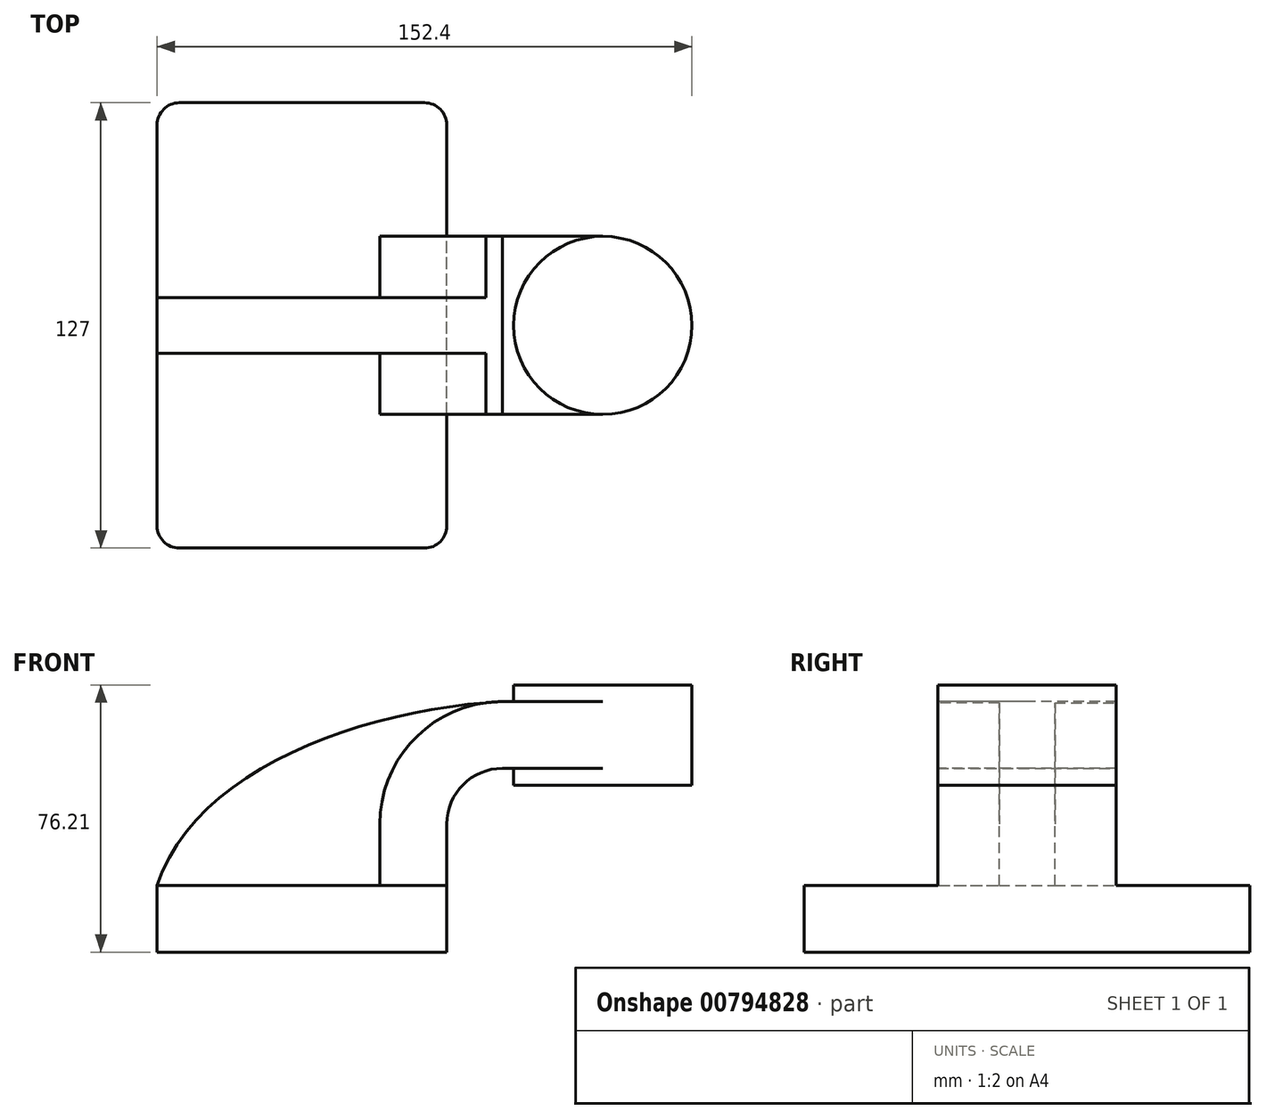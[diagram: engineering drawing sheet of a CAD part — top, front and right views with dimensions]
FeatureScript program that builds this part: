
annotation { "Feature Type Name" : "Feature", "Feature Type Description" : "" }
export const myFeature = defineFeature(function(context is Context, id is Id, definition is map)
    precondition{}
    {
        {
            var Q0;
            Q0=qCreatedBy(makeId("Front.planeOp"),FACE);
            var sketch = newSketch(context, id + "F0", { "sketchPlane" : qUnion([Q0])});
            skLineSegment(sketch, "E0.bottom", {"start": v(45.12, 9.52) * mm, "end": v(-37.43, 9.53) * mm});
            skLineSegment(sketch, "E0.top", {"start": v(45.12, -9.53) * mm, "end": v(-37.43, -9.52) * mm});
            skLineSegment(sketch, "E0.left", {"start": v(45.12, 9.53) * mm, "end": v(45.12, -9.53) * mm});
            skLineSegment(sketch, "E0.right", {"start": v(-37.43, 9.53) * mm, "end": v(-37.43, -9.53) * mm});
            skPoint(sketch, "E0.middle", {"position": v(3.84, 0) * mm});
            skLineSegment(sketch, "E1", {"start": v(45.12, 9.53) * mm, "end": v(45.12, 27) * mm});
            skArc(sketch, "E2", {"start": v(45.12, 27) * mm, "mid": v(49.76, 38.23) * mm, "end": v(61, 42.88) * mm});
            skLineSegment(sketch, "E3.bottom", {"start": v(114.97, 66.68) * mm, "end": v(64.17, 66.68) * mm});
            skLineSegment(sketch, "E3.top", {"start": v(114.97, 38.1) * mm, "end": v(64.17, 38.1) * mm});
            skLineSegment(sketch, "E3.left", {"start": v(114.97, 66.68) * mm, "end": v(114.97, 38.1) * mm});
            skLineSegment(sketch, "E3.right", {"start": v(64.17, 66.67) * mm, "end": v(64.17, 38.1) * mm});
            skPoint(sketch, "E3.middle", {"position": v(89.57, 52.39) * mm});
            skLineSegment(sketch, "E4", {"start": v(61, 42.88) * mm, "end": v(89.57, 42.88) * mm});
            skLineSegment(sketch, "E5.0", {"start": v(61, 61.93) * mm, "end": v(89.57, 61.93) * mm});
            skArc(sketch, "E5.1", {"start": v(26.07, 27) * mm, "mid": v(36.3, 51.7) * mm, "end": v(61, 61.93) * mm});
            skLineSegment(sketch, "E5.2", {"start": v(26.07, 9.52) * mm, "end": v(26.07, 27) * mm});
            skLineSegment(sketch, "E6", {"start": v(89.57, 38.1) * mm, "end": v(89.57, 66.68) * mm});
            skFitSpline(sketch, "E7", {"points": [v(-37.43, 9.53) * mm, v(61, 61.93) * mm], "startDerivative": vector(32.65, 99.26) * mm, "endDerivative": vector(120.53, 6.56) * mm});
            skSolve(sketch);
        }
        {
            var Q0;
            Q0=makeQuery(id+"F0.imprint","IMPRINT",FACE,{"disambiguationData":[TD([[makeQuery(id+"F0.imprint","IMPRINT",EDGE,{"derivedFrom":sQuery(id+"F0.wireOp",EDGE,"E0.top")}),-1.0]])]});
            extrude(context, id + "F1", {"entities" : qUnion([Q0]), "endBound" : BoundingType.SYMMETRIC, "depth" : 127 * mm, "offsetDistance" : 25.4 * mm});
        }
        {
            var Q0;
            {var subQ9=sQuery(id+"F0.wireOp",EDGE,"E1");Q0=makeQuery(id+"F0.imprint","IMPRINT",FACE,{"disambiguationData":[TD([[makeQuery(id+"F0.imprint","IMPRINT",EDGE,{"derivedFrom":subQ9}),1.0]])]});}
            var Q1;
            {var subQ0=sQuery(id+"F0.wireOp",EDGE,"E5.0");var subQ1=sQuery(id+"F0.wireOp",EDGE,"E3.right");var subQ2=makeQuery(id+"F0.imprint","INTERSECT",VERTEX,{"derivedFrom":[subQ1,subQ0]});Q1=makeQuery(id+"F0.imprint","IMPRINT",FACE,{"disambiguationData":[TD([[makeQuery(id+"F0.imprint","IMPRINT",EDGE,{"disambiguationData":[TD([[subQ2,-1.0]])],"derivedFrom":subQ1}),1.0]])]});}
            extrude(context, id + "F2", {"entities" : qUnion([Q0, Q1]), "operationType" : NewBodyOperationType.ADD, "endBound" : BoundingType.SYMMETRIC, "depth" : 50.8 * mm, "offsetDistance" : 25.4 * mm});
        }
        {
            var Q0;
            {var subQ3=sQuery(id+"F0.wireOp",EDGE,"E5.2");Q0=makeQuery(id+"F0.imprint","IMPRINT",FACE,{"disambiguationData":[TD([[makeQuery(id+"F0.imprint","IMPRINT",EDGE,{"derivedFrom":subQ3}),1.0]])]});}
            extrude(context, id + "F3", {"entities" : qUnion([Q0]), "operationType" : NewBodyOperationType.ADD, "endBound" : BoundingType.SYMMETRIC, "depth" : 15.88 * mm, "offsetDistance" : 25.4 * mm});
        }
        {
            var Q0;
            {var subQ0=sQuery(id+"F0.wireOp",EDGE,"E3.left");Q0=makeQuery(id+"F0.imprint","IMPRINT",FACE,{"disambiguationData":[TD([[makeQuery(id+"F0.imprint","IMPRINT",EDGE,{"derivedFrom":subQ0}),-1.0]])]});}
            var Q1;
            Q1=sQuery(id+"F0.wireOp",EDGE,"E6");
            revolve(context, id + "F4", {"operationType" : NewBodyOperationType.ADD, "surfaceOperationType" : NewSurfaceOperationType.NEW, "entities" : qUnion([Q0]), "axis" : qUnion([Q1]), "revolveType" : RevolveType.FULL});
        }
        {
            var Q0;
            Q0=makeQuery(id+"F1.opExtrude","CAP_EDGE",EDGE,{"disambiguationData":[OSD([sQuery(id+"F0.wireOp",EDGE,"E0.left")])],"isStart":false});
            var Q1;
            Q1=makeQuery(id+"F1.opExtrude","CAP_EDGE",EDGE,{"disambiguationData":[OSD([sQuery(id+"F0.wireOp",EDGE,"E0.right")])],"isStart":false});
            var Q2;
            Q2=makeQuery(id+"F1.opExtrude","CAP_EDGE",EDGE,{"disambiguationData":[OSD([sQuery(id+"F0.wireOp",EDGE,"E0.left")])],"isStart":true});
            var Q3;
            Q3=makeQuery(id+"F1.opExtrude","CAP_EDGE",EDGE,{"disambiguationData":[OSD([sQuery(id+"F0.wireOp",EDGE,"E0.right")])],"isStart":true});
            fillet(context, id + "F5", {"entities" : qUnion([Q0, Q1, Q2, Q3]), "radius" : 6.35 * mm, "tangentPropagation" : true, "allowEdgeOverflow" : false});
        }
    });
